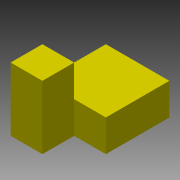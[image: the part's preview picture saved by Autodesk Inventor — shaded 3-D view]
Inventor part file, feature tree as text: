
AUTODESK INVENTOR PART (.ipt)
format: ipt  version: 2013 (Build 170138000, 138)  size: 91,136 bytes
history: native  units: in
note: dims shown in document units (in); Inventor stores cm internally (conversion verified against a paired STEP export)
features: extrude x2, sketch x2
ambient origin geometry x8: Origin, YZ Plane, XZ Plane, XY Plane, X Axis, Y Axis, Z Axis, Center Point
bodies: Solid1 (feature_tree)
feature tree (4):
  extrude  "Extrusion1"  Depth=1.5in
  extrude  "Extrusion2"  Depth=0.75in
  sketch  "Sketch1"  dims[d0=1.5in d1=1.5in]
  sketch  "Sketch2"  dims[d2=0.75in d3=0.0in d4=0.75in d5=1.5in d6=0.75in d7=0.0in]
